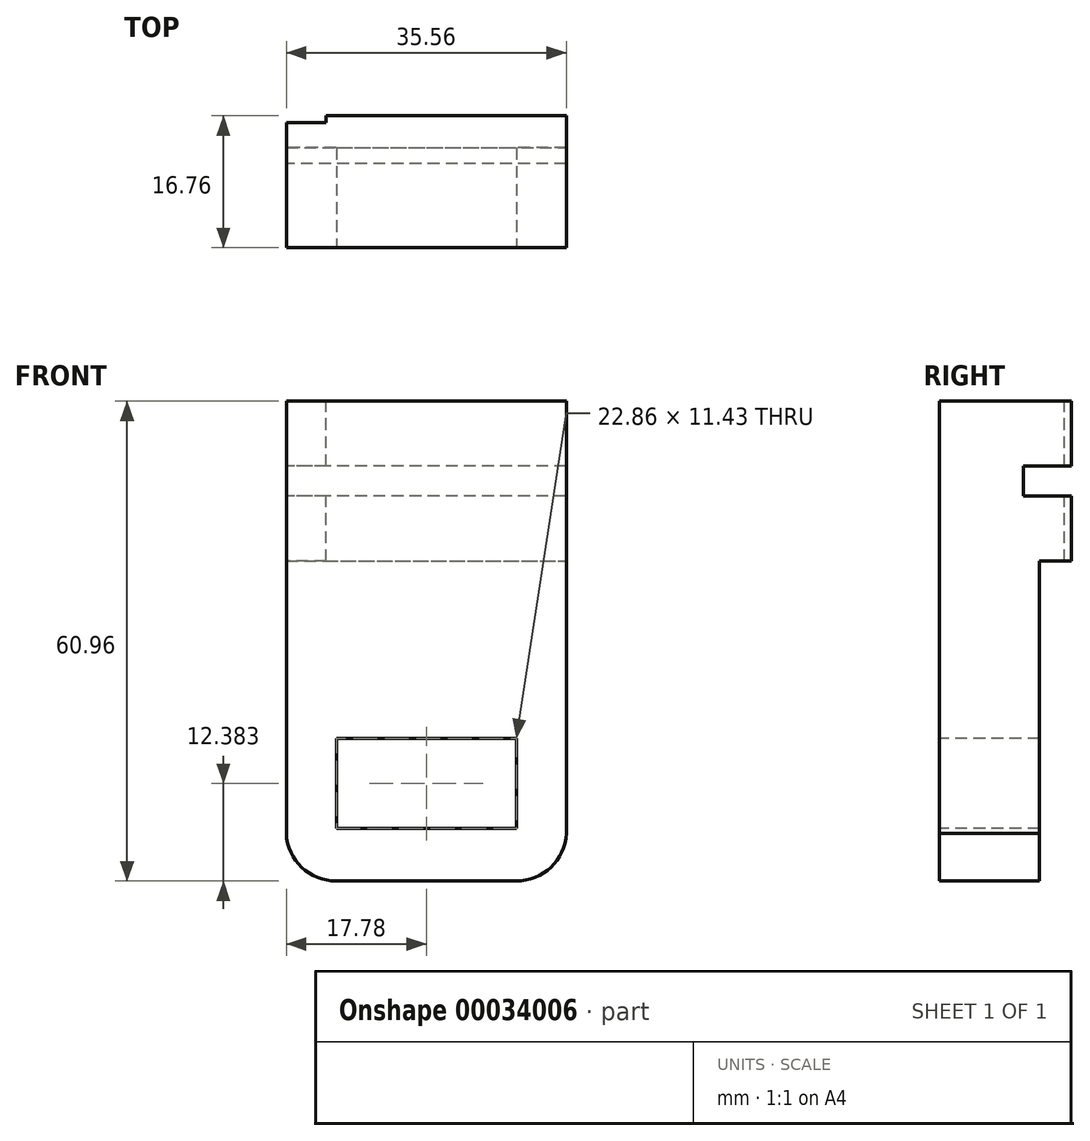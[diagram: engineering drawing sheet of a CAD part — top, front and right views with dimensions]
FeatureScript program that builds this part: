
annotation { "Feature Type Name" : "Feature", "Feature Type Description" : "" }
export const myFeature = defineFeature(function(context is Context, id is Id, definition is map)
    precondition{}
    {
        {
            var Q0;
            Q0=qCreatedBy(makeId("Front.planeOp"),FACE);
            var sketch = newSketch(context, id + "F0", { "sketchPlane" : qUnion([Q0])});
            skLineSegment(sketch, "E0.bottom", {"start": v(0, 0) * mm, "end": v(35.56, 0) * mm});
            skLineSegment(sketch, "E0.top", {"start": v(0, -55.88) * mm, "end": v(35.56, -55.88) * mm});
            skLineSegment(sketch, "E0.left", {"start": v(0, 0) * mm, "end": v(0, -55.88) * mm});
            skLineSegment(sketch, "E0.right", {"start": v(35.56, 0) * mm, "end": v(35.56, -55.88) * mm});
            skSolve(sketch);
        }
        {
            var Q0;
            Q0=makeQuery(id+"F0.imprint","IMPRINT",FACE,{"disambiguationData":[TD([[makeQuery(id+"F0.imprint","IMPRINT",EDGE,{"derivedFrom":sQuery(id+"F0.wireOp",EDGE,"E0.bottom")}),-1.0]])]});
            extrude(context, id + "F1", {"entities" : qUnion([Q0]), "depth" : 16.76 * mm});
        }
        {
            var Q0;
            Q0=makeQuery(id+"F1.opExtrude","CAP_FACE",FACE,{"disambiguationData":[OSD([sQuery(id+"F0.wireOp",EDGE,"E0.bottom"),sQuery(id+"F0.wireOp",EDGE,"E0.top"),sQuery(id+"F0.wireOp",EDGE,"E0.left"),sQuery(id+"F0.wireOp",EDGE,"E0.right")])],"isStart":false});
            var sketch = newSketch(context, id + "F2", { "sketchPlane" : qUnion([Q0])});
            skLineSegment(sketch, "E1.top", {"start": v(6.35, -54.3) * mm, "end": v(29.21, -54.3) * mm});
            skLineSegment(sketch, "E2", {"start": v(29.21, -50.8) * mm, "end": v(42.05, -50.8) * mm, "construction": true});
            skLineSegment(sketch, "E3", {"start": v(29.21, -54.3) * mm, "end": v(29.21, -42.86) * mm});
            skLineSegment(sketch, "E4", {"start": v(6.35, -54.3) * mm, "end": v(6.35, -42.86) * mm});
            skLineSegment(sketch, "E5", {"start": v(29.21, -42.86) * mm, "end": v(6.35, -42.86) * mm});
            skSolve(sketch);
        }
        {
            var Q0;
            Q0 = qSketchRegion(id + "F2", true);
            extrude(context, id + "F3", {"entities" : qUnion([Q0]), "operationType" : NewBodyOperationType.REMOVE, "endBound" : BoundingType.THROUGH_ALL, "oppositeDirection" : true, "depth" : 25.4 * mm});
        }
        {
            var Q0;
            Q0=makeQuery(id+"F1.opExtrude","CAP_FACE",FACE,{"disambiguationData":[OSD([sQuery(id+"F0.wireOp",EDGE,"E0.bottom"),sQuery(id+"F0.wireOp",EDGE,"E0.top"),sQuery(id+"F0.wireOp",EDGE,"E0.left"),sQuery(id+"F0.wireOp",EDGE,"E0.right")])],"isStart":false});
            var sketch = newSketch(context, id + "F4", { "sketchPlane" : qUnion([Q0])});
            skLineSegment(sketch, "E6.bottom", {"start": v(0, -55.88) * mm, "end": v(5.08, -55.88) * mm});
            skLineSegment(sketch, "E6.top", {"start": v(0, -20.32) * mm, "end": v(5.08, -20.32) * mm});
            skLineSegment(sketch, "E6.left", {"start": v(0, -55.88) * mm, "end": v(0, -20.32) * mm});
            skLineSegment(sketch, "E6.right", {"start": v(5.08, -55.88) * mm, "end": v(5.08, -20.32) * mm});
            skSolve(sketch);
        }
        {
            var Q0;
            Q0 = qSketchRegion(id + "F4", true);
            extrude(context, id + "F5", {"entities" : qUnion([Q0]), "operationType" : NewBodyOperationType.REMOVE, "endBound" : BoundingType.THROUGH_ALL, "oppositeDirection" : true, "depth" : 25.4 * mm});
        }
        {
            var Q0;
            Q0=makeQuery(id+"F1.opExtrude","CAP_FACE",FACE,{"disambiguationData":[OSD([sQuery(id+"F0.wireOp",EDGE,"E0.bottom"),sQuery(id+"F0.wireOp",EDGE,"E0.top"),sQuery(id+"F0.wireOp",EDGE,"E0.left"),sQuery(id+"F0.wireOp",EDGE,"E0.right")])],"isStart":true});
            var sketch = newSketch(context, id + "F6", { "sketchPlane" : qUnion([Q0])});
            skLineSegment(sketch, "E7.bottom", {"start": v(-5.08, -55.88) * mm, "end": v(-35.56, -55.88) * mm});
            skLineSegment(sketch, "E7.top", {"start": v(-5.08, -20.32) * mm, "end": v(-35.56, -20.32) * mm});
            skLineSegment(sketch, "E7.left", {"start": v(-5.08, -55.88) * mm, "end": v(-5.08, -20.32) * mm});
            skLineSegment(sketch, "E7.right", {"start": v(-35.56, -55.88) * mm, "end": v(-35.56, -20.32) * mm});
            skSolve(sketch);
        }
        {
            var Q0;
            Q0 = qSketchRegion(id + "F6", true);
            extrude(context, id + "F7", {"entities" : qUnion([Q0]), "operationType" : NewBodyOperationType.REMOVE, "oppositeDirection" : true, "depth" : 4.06 * mm});
        }
        {
            var Q0;
            Q0=makeQuery(id+"F1.opExtrude","SWEPT_FACE",FACE,{"disambiguationData":[OSD([sQuery(id+"F0.wireOp",EDGE,"E0.bottom")])]});
            var sketch = newSketch(context, id + "F8", { "sketchPlane" : qUnion([Q0])});
            skLineSegment(sketch, "E8.bottom", {"start": v(0, 0) * mm, "end": v(5.08, 0) * mm});
            skLineSegment(sketch, "E8.top", {"start": v(0, -0.89) * mm, "end": v(5.08, -0.89) * mm});
            skLineSegment(sketch, "E8.left", {"start": v(0, 0) * mm, "end": v(0, -0.89) * mm});
            skLineSegment(sketch, "E8.right", {"start": v(5.08, 0) * mm, "end": v(5.08, -0.89) * mm});
            skSolve(sketch);
        }
        {
            var Q0;
            Q0 = qSketchRegion(id + "F8", true);
            extrude(context, id + "F9", {"entities" : qUnion([Q0]), "operationType" : NewBodyOperationType.REMOVE, "endBound" : BoundingType.THROUGH_ALL, "oppositeDirection" : true, "depth" : 25.4 * mm});
        }
        {
            var Q0;
            Q0=makeQuery(id+"F1.opExtrude","SWEPT_FACE",FACE,{"disambiguationData":[OSD([sQuery(id+"F0.wireOp",EDGE,"E0.left")])]});
            var sketch = newSketch(context, id + "F10", { "sketchPlane" : qUnion([Q0])});
            skLineSegment(sketch, "E9", {"start": v(0.89, -10.16) * mm, "end": v(24.04, -10.16) * mm, "construction": true});
            skPoint(sketch, "E9.endSnap0", {"position": v(16.76, -10.16) * mm});
            skLineSegment(sketch, "E10.0", {"start": v(0.89, -12.07) * mm, "end": v(24.04, -12.07) * mm, "construction": true});
            skLineSegment(sketch, "E11.0", {"start": v(-6.88, -8.26) * mm, "end": v(24.04, -8.26) * mm, "construction": true});
            skLineSegment(sketch, "E12.right", {"start": v(6.1, -8.25) * mm, "end": v(6.1, -12.07) * mm});
            skLineSegment(sketch, "E13", {"start": v(6.1, -8.25) * mm, "end": v(-0.87, -8.26) * mm});
            skLineSegment(sketch, "E14", {"start": v(6.1, -12.07) * mm, "end": v(-0.87, -12.07) * mm});
            skLineSegment(sketch, "E15", {"start": v(-0.87, -8.26) * mm, "end": v(-0.87, -12.07) * mm});
            skSolve(sketch);
        }
        {
            var Q0;
            Q0 = qSketchRegion(id + "F10", true);
            extrude(context, id + "F11", {"entities" : qUnion([Q0]), "operationType" : NewBodyOperationType.REMOVE, "endBound" : BoundingType.THROUGH_ALL, "oppositeDirection" : true, "depth" : 25.4 * mm});
        }
        {
            var Q0;
            Q0=makeQuery(id+"F5.boolean.opBoolean","COPY",FACE,{"derivedFrom":makeQuery(id+"F5.opExtrude","SWEPT_FACE",FACE,{"disambiguationData":[OSD([sQuery(id+"F4.wireOp",EDGE,"E6.right")])]})});
            var sketch = newSketch(context, id + "F12", { "sketchPlane" : qUnion([Q0])});
            skLineSegment(sketch, "E16.0.0", {"start": v(4.06, -20.32) * mm, "end": v(4.06, -55.88) * mm});
            skLineSegment(sketch, "E16.0.1", {"start": v(4.06, -55.88) * mm, "end": v(16.76, -55.88) * mm});
            skLineSegment(sketch, "E16.0.2", {"start": v(16.76, -55.88) * mm, "end": v(16.76, -20.32) * mm});
            skLineSegment(sketch, "E16.0.3", {"start": v(16.76, -20.32) * mm, "end": v(4.06, -20.32) * mm});
            skSolve(sketch);
        }
        {
            var Q0;
            Q0=makeQuery(id+"F12.imprint","IMPRINT",FACE,{"disambiguationData":[TD([[makeQuery(id+"F12.imprint","IMPRINT",EDGE,{"derivedFrom":sQuery(id+"F12.wireOp",EDGE,"E16.0.0")}),-1.0]])]});
            var Q1;
            Q1=makeQuery(id+"F1.opExtrude","SWEPT_FACE",FACE,{"disambiguationData":[OSD([sQuery(id+"F0.wireOp",EDGE,"E0.left")])]});
            extrude(context, id + "F13", {"entities" : qUnion([Q0]), "operationType" : NewBodyOperationType.ADD, "endBound" : BoundingType.UP_TO_SURFACE, "endBoundEntityFace" : qUnion([Q1]), "depth" : 25.4 * mm});
        }
        {
            var Q0;
            Q0=makeQuery(id+"F13.boolean.opBoolean","MERGE",FACE,{"derivedFrom":[makeQuery(id+"F1.opExtrude","SWEPT_FACE",FACE,{"disambiguationData":[OSD([sQuery(id+"F0.wireOp",EDGE,"E0.top")])]}),makeQuery(id+"F13.opExtrude","SWEPT_FACE",FACE,{"disambiguationData":[OSD([sQuery(id+"F12.wireOp",EDGE,"E16.0.1")])]})]});
            var sketch = newSketch(context, id + "F14", { "sketchPlane" : qUnion([Q0])});
            skLineSegment(sketch, "E17.0.0", {"start": v(0, 4.06) * mm, "end": v(35.56, 4.06) * mm});
            skLineSegment(sketch, "E17.0.1", {"start": v(35.56, 4.06) * mm, "end": v(35.56, 16.76) * mm});
            skLineSegment(sketch, "E17.0.2", {"start": v(35.56, 16.76) * mm, "end": v(0, 16.76) * mm});
            skLineSegment(sketch, "E17.0.3", {"start": v(0, 16.76) * mm, "end": v(0, 4.06) * mm});
            skSolve(sketch);
        }
        {
            var Q0;
            Q0 = qSketchRegion(id + "F14", true);
            extrude(context, id + "F15", {"entities" : qUnion([Q0]), "operationType" : NewBodyOperationType.ADD, "depth" : 5.08 * mm});
        }
        {
            var Q0;
            Q0=makeQuery(id+"F15.boolean.opBoolean","MERGE",FACE,{"derivedFrom":[makeQuery(id+"F13.boolean.opBoolean","MERGE",FACE,{"derivedFrom":[makeQuery(id+"F1.opExtrude","CAP_FACE",FACE,{"disambiguationData":[OSD([sQuery(id+"F0.wireOp",EDGE,"E0.bottom"),sQuery(id+"F0.wireOp",EDGE,"E0.top"),sQuery(id+"F0.wireOp",EDGE,"E0.left"),sQuery(id+"F0.wireOp",EDGE,"E0.right")])],"isStart":false}),makeQuery(id+"F13.opExtrude","SWEPT_FACE",FACE,{"disambiguationData":[OSD([sQuery(id+"F12.wireOp",EDGE,"E16.0.2")])]})]}),makeQuery(id+"F15.opExtrude","SWEPT_FACE",FACE,{"disambiguationData":[OSD([sQuery(id+"F14.wireOp",EDGE,"E17.0.2")])]})]});
            var sketch = newSketch(context, id + "F16", { "sketchPlane" : qUnion([Q0])});
            skLineSegment(sketch, "E18", {"start": v(29.21, -54.3) * mm, "end": v(35.56, -54.3) * mm, "construction": true});
            skLineSegment(sketch, "E19", {"start": v(29.21, -54.3) * mm, "end": v(29.21, -60.96) * mm, "construction": true});
            skLineSegment(sketch, "E20", {"start": v(6.35, -54.3) * mm, "end": v(0, -54.3) * mm, "construction": true});
            skLineSegment(sketch, "E21", {"start": v(6.35, -54.3) * mm, "end": v(6.35, -60.96) * mm, "construction": true});
            skArc(sketch, "E22", {"start": v(0, -54.3) * mm, "mid": v(1.74, -58.99) * mm, "end": v(6.35, -60.96) * mm});
            skArc(sketch, "E23", {"start": v(29.21, -60.96) * mm, "mid": v(33.82, -58.99) * mm, "end": v(35.56, -54.3) * mm});
            skLineSegment(sketch, "E24", {"start": v(29.21, -60.96) * mm, "end": v(35.56, -60.96) * mm, "construction": true});
            skLineSegment(sketch, "E25", {"start": v(35.53, -61.07) * mm, "end": v(35.56, -54.3) * mm, "construction": true});
            skLineSegment(sketch, "E26", {"start": v(6.35, -60.96) * mm, "end": v(0, -60.96) * mm, "construction": true});
            skLineSegment(sketch, "E27", {"start": v(0, -60.96) * mm, "end": v(0, -54.3) * mm});
            skSolve(sketch);
        }
        {
            var Q0;
            Q0 = qSketchRegion(id + "F16", true);
            var Q1;
            {var subQ0=makeQuery(id+"F15.opExtrude","CAP_EDGE",EDGE,{"disambiguationData":[OSD([sQuery(id+"F14.wireOp",EDGE,"E17.0.2")])],"isStart":false});var subQ1=sQuery(id+"F16.wireOp",EDGE,"E22");var subQ2=makeQuery(id+"F16.imprint","INTERSECT",VERTEX,{"derivedFrom":[subQ0,subQ1]});Q1=makeQuery(id+"F16.imprint","IMPRINT",FACE,{"disambiguationData":[TD([[makeQuery(id+"F16.imprint","IMPRINT",EDGE,{"disambiguationData":[TD([[subQ2,1.0]])],"derivedFrom":subQ1}),-1.0]])]});}
            var Q2;
            {var subQ0=sQuery(id+"F14.wireOp",EDGE,"E17.0.2");var subQ1=makeQuery(id+"F15.opExtrude","CAP_EDGE",EDGE,{"disambiguationData":[OSD([subQ0])],"isStart":false});var subQ2=sQuery(id+"F16.wireOp",EDGE,"E23");var subQ3=makeQuery(id+"F16.imprint","INTERSECT",VERTEX,{"derivedFrom":[subQ1,sQuery(id+"F16.wireOp",EDGE,"E22"),subQ2]});Q2=makeQuery(id+"F16.imprint","IMPRINT",FACE,{"disambiguationData":[TD([[makeQuery(id+"F16.imprint","IMPRINT",EDGE,{"disambiguationData":[TD([[subQ3,-1.0]])],"derivedFrom":subQ2}),-1.0]])]});}
            extrude(context, id + "F17", {"entities" : qUnion([Q0, Q1, Q2]), "operationType" : NewBodyOperationType.REMOVE, "endBound" : BoundingType.THROUGH_ALL, "oppositeDirection" : true, "depth" : 25.4 * mm});
        }
    });
